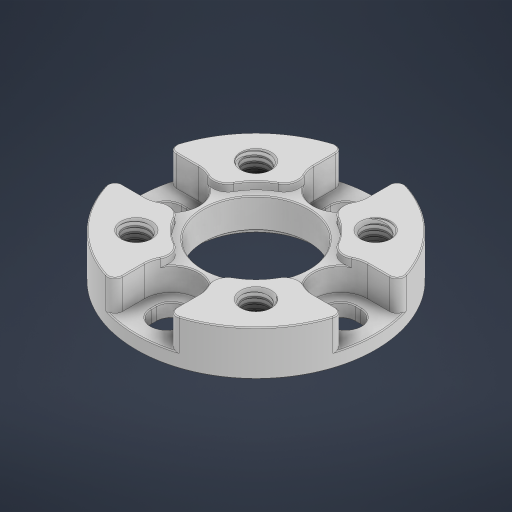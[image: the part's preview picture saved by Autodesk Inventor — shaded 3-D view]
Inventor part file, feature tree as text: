
AUTODESK INVENTOR PART (.ipt)
format: ipt  version: 2023 (Build 270158000, 158)  size: 1,229,312 bytes
history: native  units: in
note: dims shown in document units (in); Inventor stores cm internally (conversion verified against a paired STEP export)
features: chamfer x1
ambient origin geometry x8: Origin, YZ Plane, XZ Plane, XY Plane, X Axis, Y Axis, Z Axis, Center Point
bodies: Solid1 (feature_tree)
feature tree (1):
  chamfer  "Chamfer4"  [1 undecoded]
note: 1 required parameter value undecoded (feature->parameter linkage not recoverable at this tier; creation-order binding heuristic only, values carry confidence <= 0.55)
